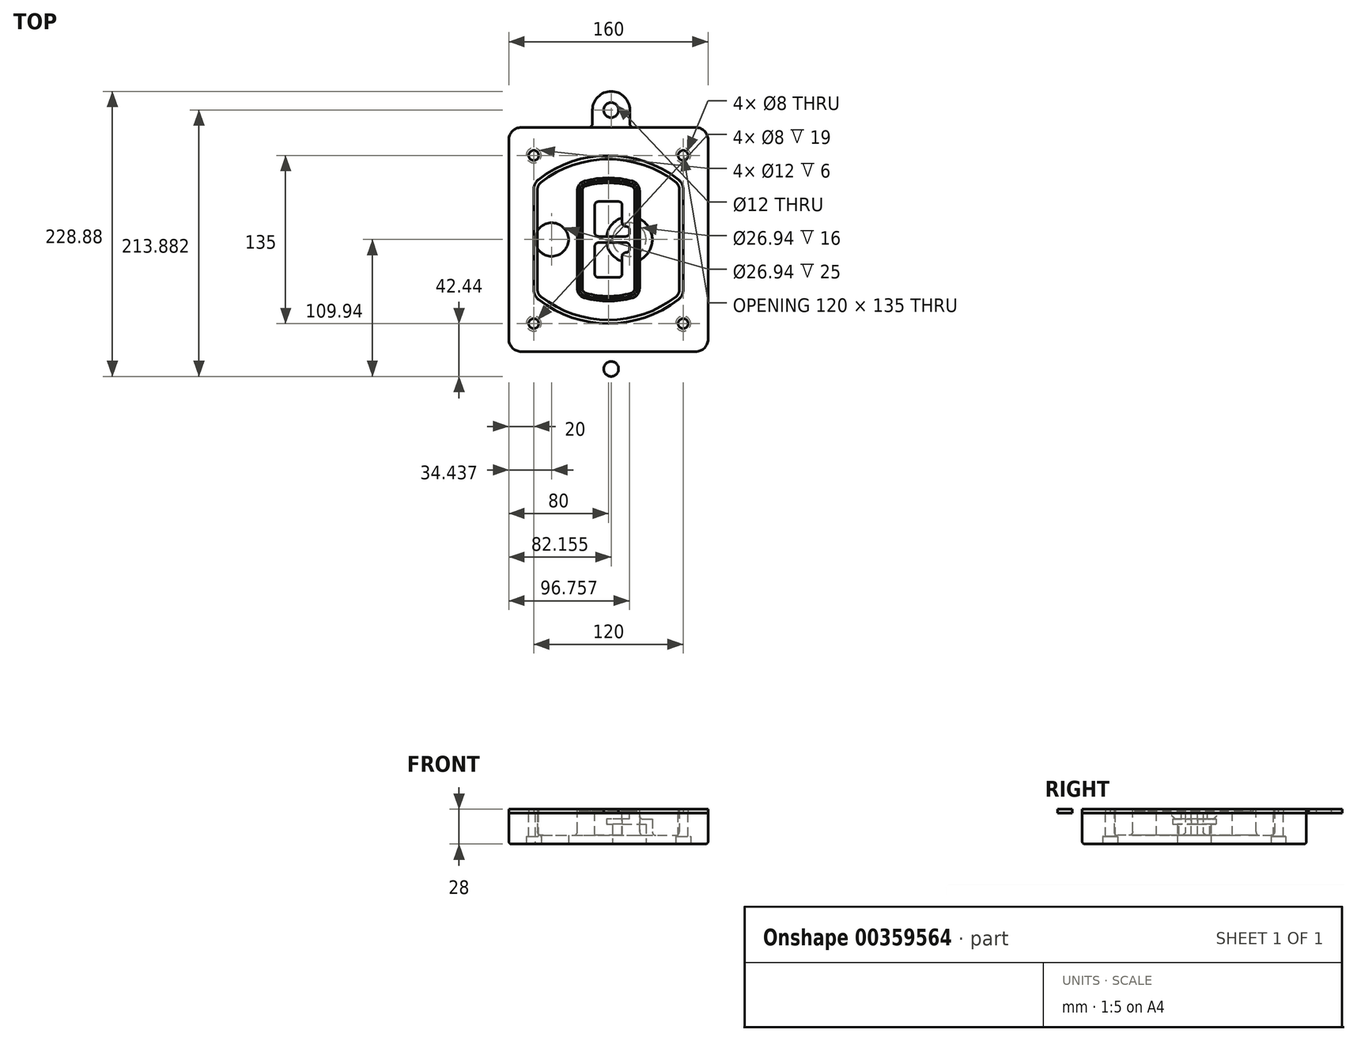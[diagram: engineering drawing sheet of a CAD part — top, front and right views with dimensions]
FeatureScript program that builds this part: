
annotation { "Feature Type Name" : "Feature", "Feature Type Description" : "" }
export const myFeature = defineFeature(function(context is Context, id is Id, definition is map)
    precondition{}
    {
        {
            var Q0;
            Q0=qCreatedBy(makeId("Top.planeOp"),FACE);
            var sketch = newSketch(context, id + "F0", { "sketchPlane" : qUnion([Q0])});
            skPoint(sketch, "E0.rect.middle", {"position": v(0, 0) * mm});
            skLineSegment(sketch, "E1.bottom", {"start": v(-70, -90) * mm, "end": v(70, -90) * mm});
            skLineSegment(sketch, "E1.top", {"start": v(-70, 90) * mm, "end": v(70, 90) * mm});
            skLineSegment(sketch, "E1.left", {"start": v(-80, -80) * mm, "end": v(-80, 80) * mm});
            skLineSegment(sketch, "E1.right", {"start": v(80, -80) * mm, "end": v(80, 80) * mm});
            skLineSegment(sketch, "E2", {"start": v(-80, 90) * mm, "end": v(80, -90) * mm, "construction": true});
            skLineSegment(sketch, "E3", {"start": v(80, 90) * mm, "end": v(-80, -90) * mm, "construction": true});
            skCircle(sketch, "E4", {"center": v(-60, 67.5) * mm, "radius": 4 * mm});
            skCircle(sketch, "E5", {"center": v(60, 67.5) * mm, "radius": 4 * mm});
            skCircle(sketch, "E6", {"center": v(60, -67.5) * mm, "radius": 4 * mm});
            skCircle(sketch, "E7", {"center": v(-60, -67.5) * mm, "radius": 4 * mm});
            skLineSegment(sketch, "E8", {"start": v(-60, 67.5) * mm, "end": v(60, 67.5) * mm, "construction": true});
            skLineSegment(sketch, "E9", {"start": v(60, 67.5) * mm, "end": v(60, -67.5) * mm, "construction": true});
            skLineSegment(sketch, "E10", {"start": v(60, -67.5) * mm, "end": v(-60, -67.5) * mm, "construction": true});
            skLineSegment(sketch, "E11", {"start": v(-60, -67.5) * mm, "end": v(-60, 67.5) * mm, "construction": true});
            skLineSegment(sketch, "E12", {"start": v(-60, 40.3) * mm, "end": v(-60, -40.3) * mm});
            skLineSegment(sketch, "E13", {"start": v(60, 40.3) * mm, "end": v(60, -40.3) * mm});
            skArc(sketch, "E14", {"start": v(56.15, 48.18) * mm, "mid": v(0, 67.5) * mm, "end": v(-56.15, 48.18) * mm});
            skArc(sketch, "E15", {"start": v(-56.15, -48.18) * mm, "mid": v(0, -67.5) * mm, "end": v(56.15, -48.18) * mm});
            skLineSegment(sketch, "E16", {"start": v(-60, 0) * mm, "end": v(60, 0) * mm, "construction": true});
            skPoint(sketch, "E17.visualSharp", {"position": v(-60, -45) * mm});
            skArc(sketch, "E17.filletArc", {"start": v(-60, -40.3) * mm, "mid": v(-58.99, -44.68) * mm, "end": v(-56.15, -48.18) * mm});
            skPoint(sketch, "E18.visualSharp", {"position": v(-60, 45) * mm});
            skArc(sketch, "E18.filletArc", {"start": v(-56.15, 48.18) * mm, "mid": v(-58.99, 44.68) * mm, "end": v(-60, 40.3) * mm});
            skPoint(sketch, "E19.visualSharp", {"position": v(60, 45) * mm});
            skArc(sketch, "E19.filletArc", {"start": v(60, 40.3) * mm, "mid": v(58.99, 44.68) * mm, "end": v(56.15, 48.18) * mm});
            skPoint(sketch, "E20.visualSharp", {"position": v(60, -45) * mm});
            skArc(sketch, "E20.filletArc", {"start": v(56.15, -48.18) * mm, "mid": v(58.99, -44.68) * mm, "end": v(60, -40.3) * mm});
            skPoint(sketch, "E21.visualSharp", {"position": v(-80, 90) * mm});
            skArc(sketch, "E21.filletArc", {"start": v(-70, 90) * mm, "mid": v(-77.07, 87.07) * mm, "end": v(-80, 80) * mm});
            skPoint(sketch, "E22.visualSharp", {"position": v(80, 90) * mm});
            skArc(sketch, "E22.filletArc", {"start": v(80, 80) * mm, "mid": v(77.07, 87.07) * mm, "end": v(70, 90) * mm});
            skPoint(sketch, "E23.visualSharp", {"position": v(80, -90) * mm});
            skArc(sketch, "E23.filletArc", {"start": v(70, -90) * mm, "mid": v(77.07, -87.07) * mm, "end": v(80, -80) * mm});
            skPoint(sketch, "E24.visualSharp", {"position": v(-80, -90) * mm});
            skArc(sketch, "E24.filletArc", {"start": v(-80, -80) * mm, "mid": v(-77.07, -87.07) * mm, "end": v(-70, -90) * mm});
            skArc(sketch, "E25.0", {"start": v(57, 40.3) * mm, "mid": v(56.3, 43.36) * mm, "end": v(54.3, 45.81) * mm});
            skLineSegment(sketch, "E25.1", {"start": v(57, 40.3) * mm, "end": v(57, -40.3) * mm});
            skArc(sketch, "E25.2", {"start": v(54.3, -45.81) * mm, "mid": v(56.3, -43.36) * mm, "end": v(57, -40.3) * mm});
            skArc(sketch, "E25.3", {"start": v(-54.3, -45.81) * mm, "mid": v(0, -64.5) * mm, "end": v(54.3, -45.81) * mm});
            skArc(sketch, "E25.4", {"start": v(-57, -40.3) * mm, "mid": v(-56.3, -43.36) * mm, "end": v(-54.3, -45.81) * mm});
            skArc(sketch, "E25.5", {"start": v(54.3, 45.81) * mm, "mid": v(0, 64.5) * mm, "end": v(-54.3, 45.81) * mm});
            skLineSegment(sketch, "E25.6", {"start": v(-57, 40.3) * mm, "end": v(-57, -40.3) * mm});
            skArc(sketch, "E25.7", {"start": v(-54.3, 45.81) * mm, "mid": v(-56.3, 43.36) * mm, "end": v(-57, 40.3) * mm});
            skArc(sketch, "E26.0", {"start": v(-58.62, 51.33) * mm, "mid": v(-62.58, 46.43) * mm, "end": v(-64, 40.3) * mm});
            skArc(sketch, "E26.1", {"start": v(58.62, 51.33) * mm, "mid": v(0, 71.5) * mm, "end": v(-58.62, 51.33) * mm});
            skArc(sketch, "E26.2", {"start": v(64, 40.3) * mm, "mid": v(62.58, 46.43) * mm, "end": v(58.62, 51.33) * mm});
            skLineSegment(sketch, "E26.3", {"start": v(64, 40.3) * mm, "end": v(64, -40.3) * mm});
            skArc(sketch, "E26.4", {"start": v(58.62, -51.33) * mm, "mid": v(62.58, -46.43) * mm, "end": v(64, -40.3) * mm});
            skLineSegment(sketch, "E26.5", {"start": v(-64, 40.3) * mm, "end": v(-64, -40.3) * mm});
            skArc(sketch, "E26.6", {"start": v(-58.62, -51.33) * mm, "mid": v(0, -71.5) * mm, "end": v(58.62, -51.33) * mm});
            skArc(sketch, "E26.7", {"start": v(-64, -40.3) * mm, "mid": v(-62.58, -46.43) * mm, "end": v(-58.62, -51.33) * mm});
            skSolve(sketch);
        }
        {
            var Q0;
            Q0=makeQuery(id+"F0.imprint","IMPRINT",FACE,{"disambiguationData":[TD([[makeQuery(id+"F0.imprint","IMPRINT",EDGE,{"derivedFrom":sQuery(id+"F0.wireOp",EDGE,"E1.bottom")}),1.0]])]});
            var Q1;
            Q1=makeQuery(id+"F0.imprint","IMPRINT",FACE,{"disambiguationData":[TD([[makeQuery(id+"F0.imprint","IMPRINT",EDGE,{"derivedFrom":sQuery(id+"F0.wireOp",EDGE,"E12")}),1.0]])]});
            var Q2;
            Q2=makeQuery(id+"F0.imprint","IMPRINT",FACE,{"disambiguationData":[TD([[makeQuery(id+"F0.imprint","IMPRINT",EDGE,{"derivedFrom":sQuery(id+"F0.wireOp",EDGE,"E25.0")}),1.0]])]});
            var Q3;
            Q3=makeQuery(id+"F0.imprint","IMPRINT",FACE,{"disambiguationData":[TD([[makeQuery(id+"F0.imprint","IMPRINT",EDGE,{"derivedFrom":sQuery(id+"F0.wireOp",EDGE,"E12")}),-1.0]])]});
            extrude(context, id + "F1", {"entities" : qUnion([Q0, Q1, Q2, Q3]), "oppositeDirection" : true, "depth" : 25 * mm});
        }
        {
            var Q0;
            Q0=makeQuery(id+"F0.imprint","IMPRINT",FACE,{"disambiguationData":[TD([[makeQuery(id+"F0.imprint","IMPRINT",EDGE,{"derivedFrom":sQuery(id+"F0.wireOp",EDGE,"E12")}),1.0]])]});
            extrude(context, id + "F2", {"entities" : qUnion([Q0]), "operationType" : NewBodyOperationType.ADD, "depth" : 3 * mm});
        }
        {
            var Q0;
            Q0=makeQuery(id+"F0.imprint","IMPRINT",FACE,{"disambiguationData":[TD([[makeQuery(id+"F0.imprint","IMPRINT",EDGE,{"derivedFrom":sQuery(id+"F0.wireOp",EDGE,"E25.0")}),1.0]])]});
            extrude(context, id + "F3", {"entities" : qUnion([Q0]), "operationType" : NewBodyOperationType.REMOVE, "oppositeDirection" : true, "depth" : 18 * mm});
        }
        {
            var Q0;
            Q0=makeQuery(id+"F2.opExtrude","CAP_FACE",FACE,{"disambiguationData":[OSD([sQuery(id+"F0.wireOp",EDGE,"E12"),sQuery(id+"F0.wireOp",EDGE,"E13"),sQuery(id+"F0.wireOp",EDGE,"E14"),sQuery(id+"F0.wireOp",EDGE,"E15"),sQuery(id+"F0.wireOp",EDGE,"E17.filletArc"),sQuery(id+"F0.wireOp",EDGE,"E18.filletArc"),sQuery(id+"F0.wireOp",EDGE,"E19.filletArc"),sQuery(id+"F0.wireOp",EDGE,"E20.filletArc"),sQuery(id+"F0.wireOp",EDGE,"E25.0"),sQuery(id+"F0.wireOp",EDGE,"E25.1"),sQuery(id+"F0.wireOp",EDGE,"E25.2"),sQuery(id+"F0.wireOp",EDGE,"E25.3"),sQuery(id+"F0.wireOp",EDGE,"E25.4"),sQuery(id+"F0.wireOp",EDGE,"E25.5"),sQuery(id+"F0.wireOp",EDGE,"E25.6"),sQuery(id+"F0.wireOp",EDGE,"E25.7")])],"isStart":false});
            var sketch = newSketch(context, id + "F4", { "sketchPlane" : qUnion([Q0])});
            skArc(sketch, "E27.0", {"start": v(-19.08, -46.97) * mm, "mid": v(0, -49.5) * mm, "end": v(19.08, -46.97) * mm});
            skArc(sketch, "E28.0", {"start": v(19.08, 46.97) * mm, "mid": v(0, 49.5) * mm, "end": v(-19.08, 46.97) * mm});
            skLineSegment(sketch, "E29", {"start": v(-25, 39.25) * mm, "end": v(-25, -39.25) * mm});
            skLineSegment(sketch, "E30", {"start": v(25, 39.25) * mm, "end": v(25, -39.25) * mm});
            skLineSegment(sketch, "E31", {"start": v(-25, 45.1) * mm, "end": v(25, 45.1) * mm, "construction": true});
            skLineSegment(sketch, "E32", {"start": v(-25, -45.1) * mm, "end": v(25, -45.1) * mm, "construction": true});
            skPoint(sketch, "E33.visualSharp", {"position": v(-25, 45.1) * mm});
            skArc(sketch, "E33.filletArc", {"start": v(-19.08, 46.97) * mm, "mid": v(-23.35, 44.11) * mm, "end": v(-25, 39.25) * mm});
            skPoint(sketch, "E34.visualSharp", {"position": v(25, 45.1) * mm});
            skArc(sketch, "E34.filletArc", {"start": v(25, 39.25) * mm, "mid": v(23.35, 44.11) * mm, "end": v(19.08, 46.97) * mm});
            skPoint(sketch, "E35.visualSharp", {"position": v(25, -45.1) * mm});
            skArc(sketch, "E35.filletArc", {"start": v(19.08, -46.97) * mm, "mid": v(23.35, -44.11) * mm, "end": v(25, -39.25) * mm});
            skPoint(sketch, "E36.visualSharp", {"position": v(-25, -45.1) * mm});
            skArc(sketch, "E36.filletArc", {"start": v(-25, -39.25) * mm, "mid": v(-23.35, -44.11) * mm, "end": v(-19.08, -46.97) * mm});
            skArc(sketch, "E37.0", {"start": v(54.3, 45.81) * mm, "mid": v(0, 64.5) * mm, "end": v(-54.3, 45.81) * mm});
            skArc(sketch, "E37.1", {"start": v(-54.3, 45.81) * mm, "mid": v(-56.3, 43.36) * mm, "end": v(-57, 40.3) * mm});
            skLineSegment(sketch, "E37.2", {"start": v(-57, 40.3) * mm, "end": v(-57, -40.3) * mm});
            skArc(sketch, "E37.3", {"start": v(-57, -40.3) * mm, "mid": v(-56.3, -43.36) * mm, "end": v(-54.3, -45.81) * mm});
            skArc(sketch, "E37.4", {"start": v(-54.3, -45.81) * mm, "mid": v(0, -64.5) * mm, "end": v(54.3, -45.81) * mm});
            skArc(sketch, "E37.5", {"start": v(54.3, -45.81) * mm, "mid": v(56.3, -43.36) * mm, "end": v(57, -40.3) * mm});
            skLineSegment(sketch, "E37.6", {"start": v(57, 40.3) * mm, "end": v(57, -40.3) * mm});
            skArc(sketch, "E37.7", {"start": v(57, 40.3) * mm, "mid": v(56.3, 43.36) * mm, "end": v(54.3, 45.81) * mm});
            skLineSegment(sketch, "E38.0", {"start": v(23, 39.25) * mm, "end": v(23, -39.25) * mm});
            skArc(sketch, "E38.1", {"start": v(18.56, -45.04) * mm, "mid": v(21.76, -42.9) * mm, "end": v(23, -39.25) * mm});
            skArc(sketch, "E38.2", {"start": v(-18.56, -45.04) * mm, "mid": v(0, -47.5) * mm, "end": v(18.56, -45.04) * mm});
            skArc(sketch, "E38.3", {"start": v(-23, -39.25) * mm, "mid": v(-21.76, -42.9) * mm, "end": v(-18.56, -45.04) * mm});
            skLineSegment(sketch, "E38.4", {"start": v(-23, 39.25) * mm, "end": v(-23, -39.25) * mm});
            skArc(sketch, "E38.5", {"start": v(23, 39.25) * mm, "mid": v(21.76, 42.9) * mm, "end": v(18.56, 45.04) * mm});
            skArc(sketch, "E38.6", {"start": v(-18.56, 45.04) * mm, "mid": v(-21.76, 42.9) * mm, "end": v(-23, 39.25) * mm});
            skArc(sketch, "E38.7", {"start": v(18.56, 45.04) * mm, "mid": v(0, 47.5) * mm, "end": v(-18.56, 45.04) * mm});
            skArc(sketch, "E39.0", {"start": v(21, 39.25) * mm, "mid": v(20.18, 41.68) * mm, "end": v(18.04, 43.1) * mm});
            skLineSegment(sketch, "E39.1", {"start": v(21, 39.25) * mm, "end": v(21, -39.25) * mm});
            skArc(sketch, "E39.2", {"start": v(18.04, -43.1) * mm, "mid": v(20.18, -41.68) * mm, "end": v(21, -39.25) * mm});
            skArc(sketch, "E39.3", {"start": v(-18.04, -43.1) * mm, "mid": v(0, -45.5) * mm, "end": v(18.04, -43.1) * mm});
            skArc(sketch, "E39.4", {"start": v(-21, -39.25) * mm, "mid": v(-20.18, -41.68) * mm, "end": v(-18.04, -43.1) * mm});
            skArc(sketch, "E39.5", {"start": v(18.04, 43.1) * mm, "mid": v(0, 45.5) * mm, "end": v(-18.04, 43.1) * mm});
            skLineSegment(sketch, "E39.6", {"start": v(-21, 39.25) * mm, "end": v(-21, -39.25) * mm});
            skArc(sketch, "E39.7", {"start": v(-18.04, 43.1) * mm, "mid": v(-20.18, 41.68) * mm, "end": v(-21, 39.25) * mm});
            skLineSegment(sketch, "E40", {"start": v(-25, 0) * mm, "end": v(25, 0) * mm, "construction": true});
            skLineSegment(sketch, "E41", {"start": v(-11, 5.5) * mm, "end": v(-11, 27.5) * mm});
            skLineSegment(sketch, "E42", {"start": v(-8, 30.5) * mm, "end": v(8, 30.5) * mm});
            skLineSegment(sketch, "E43", {"start": v(11, 27.5) * mm, "end": v(11, 13.5) * mm});
            skLineSegment(sketch, "E44", {"start": v(14, 10.5) * mm, "end": v(14, 10.5) * mm});
            skLineSegment(sketch, "E45", {"start": v(17, 7.5) * mm, "end": v(17, 5.5) * mm});
            skLineSegment(sketch, "E46", {"start": v(14, 2.5) * mm, "end": v(-8, 2.5) * mm});
            skPoint(sketch, "E47.visualSharp", {"position": v(-11, 30.5) * mm});
            skArc(sketch, "E47.filletArc", {"start": v(-8, 30.5) * mm, "mid": v(-10.12, 29.62) * mm, "end": v(-11, 27.5) * mm});
            skPoint(sketch, "E48.visualSharp", {"position": v(11, 30.5) * mm});
            skArc(sketch, "E48.filletArc", {"start": v(11, 27.5) * mm, "mid": v(10.12, 29.62) * mm, "end": v(8, 30.5) * mm});
            skPoint(sketch, "E49.visualSharp", {"position": v(11, 10.5) * mm});
            skArc(sketch, "E49.filletArc", {"start": v(11, 13.5) * mm, "mid": v(11.88, 11.38) * mm, "end": v(14, 10.5) * mm});
            skPoint(sketch, "E50.visualSharp", {"position": v(17, 10.5) * mm});
            skArc(sketch, "E50.filletArc", {"start": v(17, 7.5) * mm, "mid": v(16.12, 9.62) * mm, "end": v(14, 10.5) * mm});
            skPoint(sketch, "E51.visualSharp", {"position": v(17, 2.5) * mm});
            skArc(sketch, "E51.filletArc", {"start": v(14, 2.5) * mm, "mid": v(16.12, 3.38) * mm, "end": v(17, 5.5) * mm});
            skPoint(sketch, "E52.visualSharp", {"position": v(-11, 2.5) * mm});
            skArc(sketch, "E52.filletArc", {"start": v(-11, 5.5) * mm, "mid": v(-10.12, 3.38) * mm, "end": v(-8, 2.5) * mm});
            skLineSegment(sketch, "E53.0.MirrorCS", {"start": v(14, -2.5) * mm, "end": v(-8, -2.5) * mm});
            skArc(sketch, "E54.0.MirrorCS", {"start": v(-11, -5.5) * mm, "mid": v(-10.12, -3.38) * mm, "end": v(-8, -2.5) * mm});
            skLineSegment(sketch, "E55.0.MirrorCS", {"start": v(-11, -5.5) * mm, "end": v(-11, -27.5) * mm});
            skArc(sketch, "E56.0.MirrorCS", {"start": v(-8, -30.5) * mm, "mid": v(-10.12, -29.62) * mm, "end": v(-11, -27.5) * mm});
            skLineSegment(sketch, "E57.0.MirrorCS", {"start": v(-8, -30.5) * mm, "end": v(8, -30.5) * mm});
            skArc(sketch, "E58.0.MirrorCS", {"start": v(11, -27.5) * mm, "mid": v(10.12, -29.62) * mm, "end": v(8, -30.5) * mm});
            skLineSegment(sketch, "E59.0.MirrorCS", {"start": v(11, -27.5) * mm, "end": v(11, -13.5) * mm});
            skArc(sketch, "E60.0.MirrorCS", {"start": v(11, -13.5) * mm, "mid": v(11.88, -11.38) * mm, "end": v(14, -10.5) * mm});
            skArc(sketch, "E61.0.MirrorCS", {"start": v(17, -7.5) * mm, "mid": v(16.12, -9.62) * mm, "end": v(14, -10.5) * mm});
            skLineSegment(sketch, "E62.0.MirrorCS", {"start": v(17, -7.5) * mm, "end": v(17, -5.5) * mm});
            skArc(sketch, "E63.0.MirrorCS", {"start": v(14, -2.5) * mm, "mid": v(16.12, -3.38) * mm, "end": v(17, -5.5) * mm});
            skSolve(sketch);
        }
        {
            var Q0;
            Q0=makeQuery(id+"F4.imprint","IMPRINT",FACE,{"disambiguationData":[TD([[makeQuery(id+"F4.imprint","IMPRINT",EDGE,{"derivedFrom":sQuery(id+"F4.wireOp",EDGE,"E27.0")}),1.0]])]});
            var Q1;
            Q1=makeQuery(id+"F4.imprint","IMPRINT",FACE,{"disambiguationData":[TD([[makeQuery(id+"F4.imprint","IMPRINT",EDGE,{"derivedFrom":sQuery(id+"F4.wireOp",EDGE,"E38.0")}),-1.0]])]});
            var Q2;
            Q2=makeQuery(id+"F4.imprint","IMPRINT",FACE,{"disambiguationData":[TD([[makeQuery(id+"F4.imprint","IMPRINT",EDGE,{"derivedFrom":sQuery(id+"F4.wireOp",EDGE,"E39.0")}),1.0]])]});
            extrude(context, id + "F5", {"entities" : qUnion([Q0, Q1, Q2]), "operationType" : NewBodyOperationType.ADD, "endBound" : BoundingType.UP_TO_NEXT, "oppositeDirection" : true, "depth" : 25 * mm});
        }
        {
            var Q0;
            Q0=makeQuery(id+"F4.imprint","IMPRINT",FACE,{"disambiguationData":[TD([[makeQuery(id+"F4.imprint","IMPRINT",EDGE,{"derivedFrom":sQuery(id+"F4.wireOp",EDGE,"E38.0")}),-1.0]])]});
            extrude(context, id + "F6", {"entities" : qUnion([Q0]), "operationType" : NewBodyOperationType.REMOVE, "oppositeDirection" : true, "depth" : 2 * mm});
        }
        {
            var Q0;
            Q0=makeQuery(id+"F1.opExtrude","CAP_FACE",FACE,{"disambiguationData":[OSD([sQuery(id+"F0.wireOp",EDGE,"E1.bottom"),sQuery(id+"F0.wireOp",EDGE,"E1.top"),sQuery(id+"F0.wireOp",EDGE,"E1.left"),sQuery(id+"F0.wireOp",EDGE,"E1.right"),sQuery(id+"F0.wireOp",EDGE,"E4"),sQuery(id+"F0.wireOp",EDGE,"E5"),sQuery(id+"F0.wireOp",EDGE,"E6"),sQuery(id+"F0.wireOp",EDGE,"E7"),sQuery(id+"F0.wireOp",EDGE,"E21.filletArc"),sQuery(id+"F0.wireOp",EDGE,"E22.filletArc"),sQuery(id+"F0.wireOp",EDGE,"E23.filletArc"),sQuery(id+"F0.wireOp",EDGE,"E24.filletArc")])],"isStart":false});
            var sketch = newSketch(context, id + "F7", { "sketchPlane" : qUnion([Q0])});
            skCircle(sketch, "E64", {"center": v(16.76, 0) * mm, "radius": 13.47 * mm});
            skCircle(sketch, "E65", {"center": v(-45.56, 0) * mm, "radius": 13.47 * mm});
            skLineSegment(sketch, "E66", {"start": v(80, 0) * mm, "end": v(-80, 0) * mm});
            skCircle(sketch, "E67", {"center": v(16.76, 0) * mm, "radius": 18.47 * mm});
            skCircle(sketch, "E68", {"center": v(60, -67.5) * mm, "radius": 6 * mm});
            skCircle(sketch, "E69", {"center": v(-60, -67.5) * mm, "radius": 6 * mm});
            skCircle(sketch, "E70", {"center": v(-60, 67.5) * mm, "radius": 6 * mm});
            skCircle(sketch, "E71", {"center": v(60, 67.5) * mm, "radius": 6 * mm});
            skSolve(sketch);
        }
        {
            var Q0;
            {var subQ1=sQuery(id+"F7.wireOp",EDGE,"E66");var subQ4=sQuery(id+"F7.wireOp",EDGE,"E64");var subQ6=makeQuery(id+"F7.imprint","INTERSECT",VERTEX,{"disambiguationData":[OD(0.0)],"derivedFrom":[subQ4,subQ1]});Q0=makeQuery(id+"F7.imprint","IMPRINT",FACE,{"disambiguationData":[TD([[makeQuery(id+"F7.imprint","IMPRINT",EDGE,{"disambiguationData":[TD([[subQ6,-1.0]])],"derivedFrom":subQ4}),-1.0]])]});}
            var Q1;
            {var subQ0=sQuery(id+"F7.wireOp",EDGE,"E66");var subQ1=sQuery(id+"F7.wireOp",EDGE,"E64");var subQ3=makeQuery(id+"F7.imprint","INTERSECT",VERTEX,{"disambiguationData":[OD(0.0)],"derivedFrom":[subQ1,subQ0]});Q1=makeQuery(id+"F7.imprint","IMPRINT",FACE,{"disambiguationData":[TD([[makeQuery(id+"F7.imprint","IMPRINT",EDGE,{"disambiguationData":[TD([[subQ3,-1.0]])],"derivedFrom":subQ1}),1.0]])]});}
            var Q2;
            {var subQ0=sQuery(id+"F7.wireOp",EDGE,"E66");var subQ1=sQuery(id+"F7.wireOp",EDGE,"E64");var subQ3=makeQuery(id+"F7.imprint","INTERSECT",VERTEX,{"disambiguationData":[OD(0.0)],"derivedFrom":[subQ1,subQ0]});Q2=makeQuery(id+"F7.imprint","IMPRINT",FACE,{"disambiguationData":[TD([[makeQuery(id+"F7.imprint","IMPRINT",EDGE,{"disambiguationData":[TD([[subQ3,1.0]])],"derivedFrom":subQ1}),1.0]])]});}
            var Q3;
            {var subQ1=sQuery(id+"F7.wireOp",EDGE,"E66");var subQ4=sQuery(id+"F7.wireOp",EDGE,"E64");var subQ6=makeQuery(id+"F7.imprint","INTERSECT",VERTEX,{"disambiguationData":[OD(0.0)],"derivedFrom":[subQ4,subQ1]});Q3=makeQuery(id+"F7.imprint","IMPRINT",FACE,{"disambiguationData":[TD([[makeQuery(id+"F7.imprint","IMPRINT",EDGE,{"disambiguationData":[TD([[subQ6,1.0]])],"derivedFrom":subQ4}),-1.0]])]});}
            extrude(context, id + "F8", {"entities" : qUnion([Q0, Q1, Q2, Q3]), "operationType" : NewBodyOperationType.ADD, "oppositeDirection" : true, "depth" : 20 * mm});
        }
        {
            var Q0;
            {var subQ0=sQuery(id+"F7.wireOp",EDGE,"E66");var subQ1=sQuery(id+"F7.wireOp",EDGE,"E64");var subQ3=makeQuery(id+"F7.imprint","INTERSECT",VERTEX,{"disambiguationData":[OD(0.0)],"derivedFrom":[subQ1,subQ0]});Q0=makeQuery(id+"F7.imprint","IMPRINT",FACE,{"disambiguationData":[TD([[makeQuery(id+"F7.imprint","IMPRINT",EDGE,{"disambiguationData":[TD([[subQ3,-1.0]])],"derivedFrom":subQ1}),1.0]])]});}
            var Q1;
            {var subQ0=sQuery(id+"F7.wireOp",EDGE,"E66");var subQ1=sQuery(id+"F7.wireOp",EDGE,"E64");var subQ3=makeQuery(id+"F7.imprint","INTERSECT",VERTEX,{"disambiguationData":[OD(0.0)],"derivedFrom":[subQ1,subQ0]});Q1=makeQuery(id+"F7.imprint","IMPRINT",FACE,{"disambiguationData":[TD([[makeQuery(id+"F7.imprint","IMPRINT",EDGE,{"disambiguationData":[TD([[subQ3,1.0]])],"derivedFrom":subQ1}),1.0]])]});}
            extrude(context, id + "F9", {"entities" : qUnion([Q0, Q1]), "operationType" : NewBodyOperationType.REMOVE, "oppositeDirection" : true, "depth" : 16 * mm});
        }
        {
            var Q0;
            {var subQ0=sQuery(id+"F7.wireOp",EDGE,"E66");var subQ1=sQuery(id+"F7.wireOp",EDGE,"E65");var subQ3=makeQuery(id+"F7.imprint","INTERSECT",VERTEX,{"disambiguationData":[OD(0.0)],"derivedFrom":[subQ1,subQ0]});Q0=makeQuery(id+"F7.imprint","IMPRINT",FACE,{"disambiguationData":[TD([[makeQuery(id+"F7.imprint","IMPRINT",EDGE,{"disambiguationData":[TD([[subQ3,-1.0]])],"derivedFrom":subQ1}),1.0]])]});}
            var Q1;
            {var subQ0=sQuery(id+"F7.wireOp",EDGE,"E66");var subQ1=sQuery(id+"F7.wireOp",EDGE,"E65");var subQ3=makeQuery(id+"F7.imprint","INTERSECT",VERTEX,{"disambiguationData":[OD(0.0)],"derivedFrom":[subQ1,subQ0]});Q1=makeQuery(id+"F7.imprint","IMPRINT",FACE,{"disambiguationData":[TD([[makeQuery(id+"F7.imprint","IMPRINT",EDGE,{"disambiguationData":[TD([[subQ3,1.0]])],"derivedFrom":subQ1}),1.0]])]});}
            extrude(context, id + "F10", {"entities" : qUnion([Q0, Q1]), "operationType" : NewBodyOperationType.REMOVE, "oppositeDirection" : true, "depth" : 25 * mm});
        }
        {
            var Q0;
            Q0=makeQuery(id+"F7.imprint","IMPRINT",FACE,{"disambiguationData":[TD([[makeQuery(id+"F7.imprint","IMPRINT",EDGE,{"derivedFrom":sQuery(id+"F7.wireOp",EDGE,"E68")}),1.0]])]});
            var Q1;
            Q1=makeQuery(id+"F7.imprint","IMPRINT",FACE,{"disambiguationData":[TD([[makeQuery(id+"F7.imprint","IMPRINT",EDGE,{"derivedFrom":makeQuery(id+"F1.opExtrude","CAP_EDGE",EDGE,{"disambiguationData":[OSD([sQuery(id+"F0.wireOp",EDGE,"E5")])],"isStart":false})}),-1.0]])]});
            var Q2;
            Q2=makeQuery(id+"F7.imprint","IMPRINT",FACE,{"disambiguationData":[TD([[makeQuery(id+"F7.imprint","IMPRINT",EDGE,{"derivedFrom":sQuery(id+"F7.wireOp",EDGE,"E69")}),1.0]])]});
            var Q3;
            Q3=makeQuery(id+"F7.imprint","IMPRINT",FACE,{"disambiguationData":[TD([[makeQuery(id+"F7.imprint","IMPRINT",EDGE,{"derivedFrom":makeQuery(id+"F1.opExtrude","CAP_EDGE",EDGE,{"disambiguationData":[OSD([sQuery(id+"F0.wireOp",EDGE,"E4")])],"isStart":false})}),-1.0]])]});
            var Q4;
            Q4=makeQuery(id+"F7.imprint","IMPRINT",FACE,{"disambiguationData":[TD([[makeQuery(id+"F7.imprint","IMPRINT",EDGE,{"derivedFrom":sQuery(id+"F7.wireOp",EDGE,"E70")}),1.0]])]});
            var Q5;
            Q5=makeQuery(id+"F7.imprint","IMPRINT",FACE,{"disambiguationData":[TD([[makeQuery(id+"F7.imprint","IMPRINT",EDGE,{"derivedFrom":makeQuery(id+"F1.opExtrude","CAP_EDGE",EDGE,{"disambiguationData":[OSD([sQuery(id+"F0.wireOp",EDGE,"E7")])],"isStart":false})}),-1.0]])]});
            var Q6;
            Q6=makeQuery(id+"F7.imprint","IMPRINT",FACE,{"disambiguationData":[TD([[makeQuery(id+"F7.imprint","IMPRINT",EDGE,{"derivedFrom":sQuery(id+"F7.wireOp",EDGE,"E71")}),1.0]])]});
            var Q7;
            Q7=makeQuery(id+"F7.imprint","IMPRINT",FACE,{"disambiguationData":[TD([[makeQuery(id+"F7.imprint","IMPRINT",EDGE,{"derivedFrom":makeQuery(id+"F1.opExtrude","CAP_EDGE",EDGE,{"disambiguationData":[OSD([sQuery(id+"F0.wireOp",EDGE,"E6")])],"isStart":false})}),-1.0]])]});
            extrude(context, id + "F11", {"entities" : qUnion([Q0, Q1, Q2, Q3, Q4, Q5, Q6, Q7]), "operationType" : NewBodyOperationType.REMOVE, "oppositeDirection" : true, "depth" : 6 * mm});
        }
        {
            var Q0;
            Q0=makeQuery(id+"F9.boolean.opBoolean","COPY",FACE,{"derivedFrom":makeQuery(id+"F9.opExtrude","CAP_FACE",FACE,{"disambiguationData":[OSD([sQuery(id+"F7.wireOp",EDGE,"E64")])],"isStart":false})});
            var sketch = newSketch(context, id + "F12", { "sketchPlane" : qUnion([Q0])});
            skArc(sketch, "E72.0", {"start": v(11, 17.55) * mm, "mid": v(2.57, 11.82) * mm, "end": v(-1.54, 2.5) * mm});
            skArc(sketch, "E72.1", {"start": v(-1.54, -2.5) * mm, "mid": v(2.57, -11.82) * mm, "end": v(11, -17.55) * mm});
            skLineSegment(sketch, "E73", {"start": v(-1.54, -2.5) * mm, "end": v(14, -2.5) * mm});
            skLineSegment(sketch, "E74.0", {"start": v(14, 2.5) * mm, "end": v(-1.54, 2.5) * mm});
            skArc(sketch, "E74.1", {"start": v(14, 2.5) * mm, "mid": v(16.12, 3.38) * mm, "end": v(17, 5.5) * mm});
            skLineSegment(sketch, "E74.2", {"start": v(17, 7.5) * mm, "end": v(17, 5.5) * mm});
            skArc(sketch, "E74.3", {"start": v(17, 7.5) * mm, "mid": v(16.12, 9.62) * mm, "end": v(14, 10.5) * mm});
            skArc(sketch, "E74.4", {"start": v(11, 13.5) * mm, "mid": v(11.88, 11.38) * mm, "end": v(14, 10.5) * mm});
            skLineSegment(sketch, "E74.5", {"start": v(11, 17.55) * mm, "end": v(11, 13.5) * mm});
            skLineSegment(sketch, "E74.7", {"start": v(14, -2.5) * mm, "end": v(-1.54, -2.5) * mm});
            skArc(sketch, "E74.8", {"start": v(14, -2.5) * mm, "mid": v(16.12, -3.38) * mm, "end": v(17, -5.5) * mm});
            skLineSegment(sketch, "E74.9", {"start": v(17, -7.5) * mm, "end": v(17, -5.5) * mm});
            skArc(sketch, "E74.10", {"start": v(17, -7.5) * mm, "mid": v(16.12, -9.62) * mm, "end": v(14, -10.5) * mm});
            skArc(sketch, "E74.11", {"start": v(11, -13.5) * mm, "mid": v(11.88, -11.38) * mm, "end": v(14, -10.5) * mm});
            skLineSegment(sketch, "E74.12", {"start": v(11, -17.55) * mm, "end": v(11, -13.5) * mm});
            skPoint(sketch, "E75.orphan", {"position": v(11, -27.5) * mm});
            skPoint(sketch, "E76.orphan", {"position": v(-8, -2.5) * mm});
            skPoint(sketch, "E77.orphan", {"position": v(-8, 2.5) * mm});
            skPoint(sketch, "E78.orphan", {"position": v(11, 27.5) * mm});
            skSolve(sketch);
        }
        {
            var Q0;
            {var subQ7=sQuery(id+"F12.wireOp",EDGE,"E72.0");var subQ14=sQuery(id+"F12.wireOp",EDGE,"E72.1");var subQ16=sQuery(id+"F12.wireOp",EDGE,"E74.1");var subQ18=sQuery(id+"F12.wireOp",EDGE,"E74.8");Q0=qUnion([makeQuery(id+"F12.imprint","IMPRINT",FACE,{"disambiguationData":[TD([[makeQuery(id+"F12.imprint","IMPRINT",EDGE,{"derivedFrom":subQ7}),1.0]])]}),makeQuery(id+"F12.imprint","IMPRINT",FACE,{"disambiguationData":[TD([[makeQuery(id+"F12.imprint","IMPRINT",EDGE,{"derivedFrom":subQ14}),1.0]])]}),makeQuery(id+"F12.imprint","IMPRINT",FACE,{"disambiguationData":[TD([[makeQuery(id+"F12.imprint","IMPRINT",EDGE,{"derivedFrom":subQ16}),1.0]])]}),makeQuery(id+"F12.imprint","IMPRINT",FACE,{"disambiguationData":[TD([[makeQuery(id+"F12.imprint","IMPRINT",EDGE,{"derivedFrom":subQ18}),-1.0]])]})]);}
            var Q1;
            Q1=makeQuery(id+"F5.boolean.opBoolean","SPLIT",FACE,{"disambiguationData":[TD([makeQuery(id+"F5.opExtrude","SWEPT_FACE",FACE,{"disambiguationData":[OSD([sQuery(id+"F4.wireOp",EDGE,"E41")])]})])],"derivedFrom":makeQuery(id+"F3.boolean.opBoolean","COPY",FACE,{"derivedFrom":makeQuery(id+"F3.opExtrude","CAP_FACE",FACE,{"disambiguationData":[OSD([sQuery(id+"F0.wireOp",EDGE,"E25.0"),sQuery(id+"F0.wireOp",EDGE,"E25.1"),sQuery(id+"F0.wireOp",EDGE,"E25.2"),sQuery(id+"F0.wireOp",EDGE,"E25.3"),sQuery(id+"F0.wireOp",EDGE,"E25.4"),sQuery(id+"F0.wireOp",EDGE,"E25.5"),sQuery(id+"F0.wireOp",EDGE,"E25.6"),sQuery(id+"F0.wireOp",EDGE,"E25.7")])],"isStart":false})})});
            extrude(context, id + "F13", {"entities" : qUnion([Q0]), "operationType" : NewBodyOperationType.REMOVE, "endBound" : BoundingType.UP_TO_SURFACE, "endBoundEntityFace" : qUnion([Q1]), "depth" : 25 * mm});
        }
        {
            var Q0;
            Q0=makeQuery(id+"F3.boolean.opBoolean","COPY",EDGE,{"derivedFrom":makeQuery(id+"F3.opExtrude","CAP_EDGE",EDGE,{"disambiguationData":[OSD([sQuery(id+"F0.wireOp",EDGE,"E25.6")])],"isStart":false})});
            var Q1;
            Q1=makeQuery(id+"F8.boolean.opBoolean","INTERSECT",EDGE,{"derivedFrom":[makeQuery(id+"F5.opExtrude","SWEPT_FACE",FACE,{"disambiguationData":[OSD([sQuery(id+"F4.wireOp",EDGE,"E30")])]}),makeQuery(id+"F8.opExtrude","CAP_FACE",FACE,{"disambiguationData":[OSD([sQuery(id+"F7.wireOp",EDGE,"E67")])],"isStart":false})]});
            var Q2;
            Q2=makeQuery(id+"F8.boolean.opBoolean","INTERSECT",EDGE,{"disambiguationData":[OD(1.0)],"derivedFrom":[makeQuery(id+"F5.opExtrude","SWEPT_FACE",FACE,{"disambiguationData":[OSD([sQuery(id+"F4.wireOp",EDGE,"E30")])]}),makeQuery(id+"F8.opExtrude","SWEPT_FACE",FACE,{"disambiguationData":[OSD([sQuery(id+"F7.wireOp",EDGE,"E67")])]})]});
            var Q3;
            {var subQ0=sQuery(id+"F4.wireOp",EDGE,"E30");Q3=makeQuery(id+"F8.boolean.opBoolean","SPLIT",EDGE,{"disambiguationData":[TD([makeQuery(id+"F5.opExtrude","SWEPT_FACE",FACE,{"disambiguationData":[OSD([sQuery(id+"F4.wireOp",EDGE,"E35.filletArc")])]})])],"derivedFrom":makeQuery(id+"F5.opExtrude","CAP_EDGE",EDGE,{"disambiguationData":[OSD([subQ0])],"isStart":false})});}
            var Q4;
            {var subQ0=sQuery(id+"F0.wireOp",EDGE,"E25.7");var subQ1=sQuery(id+"F0.wireOp",EDGE,"E25.1");var subQ2=sQuery(id+"F0.wireOp",EDGE,"E25.6");var subQ3=sQuery(id+"F0.wireOp",EDGE,"E25.5");var subQ4=sQuery(id+"F0.wireOp",EDGE,"E25.4");var subQ5=sQuery(id+"F0.wireOp",EDGE,"E25.0");var subQ6=sQuery(id+"F0.wireOp",EDGE,"E25.2");var subQ7=sQuery(id+"F0.wireOp",EDGE,"E25.3");Q4=makeQuery(id+"F8.boolean.opBoolean","INTERSECT",EDGE,{"derivedFrom":[makeQuery(id+"F5.boolean.opBoolean","SPLIT",FACE,{"disambiguationData":[TD([makeQuery(id+"F2.opExtrude","SWEPT_FACE",FACE,{"disambiguationData":[OSD([subQ5])]})])],"derivedFrom":makeQuery(id+"F3.boolean.opBoolean","COPY",FACE,{"derivedFrom":makeQuery(id+"F3.opExtrude","CAP_FACE",FACE,{"disambiguationData":[OSD([subQ5,subQ1,subQ6,subQ7,subQ4,subQ3,subQ2,subQ0])],"isStart":false})})}),makeQuery(id+"F8.opExtrude","SWEPT_FACE",FACE,{"disambiguationData":[OSD([sQuery(id+"F7.wireOp",EDGE,"E67")])]})]});}
            var Q5;
            Q5=makeQuery(id+"F8.boolean.opBoolean","INTERSECT",EDGE,{"disambiguationData":[OD(0.0)],"derivedFrom":[makeQuery(id+"F5.opExtrude","SWEPT_FACE",FACE,{"disambiguationData":[OSD([sQuery(id+"F4.wireOp",EDGE,"E30")])]}),makeQuery(id+"F8.opExtrude","SWEPT_FACE",FACE,{"disambiguationData":[OSD([sQuery(id+"F7.wireOp",EDGE,"E67")])]})]});
            fillet(context, id + "F14", {"entities" : qUnion([Q0, Q1, Q2, Q3, Q4, Q5]), "radius" : 3 * mm, "tangentPropagation" : true, "allowEdgeOverflow" : false});
        }
        {
            var Q0;
            Q0=makeQuery(id+"F1.opExtrude","CAP_EDGE",EDGE,{"disambiguationData":[OSD([sQuery(id+"F0.wireOp",EDGE,"E1.bottom")])],"isStart":false});
            fillet(context, id + "F15", {"entities" : qUnion([Q0]), "radius" : 2 * mm, "tangentPropagation" : true, "allowEdgeOverflow" : false});
        }
        {
            var Q0;
            {var subQ0=sQuery(id+"F0.wireOp",EDGE,"E21.filletArc");var subQ1=sQuery(id+"F0.wireOp",EDGE,"E7");var subQ2=sQuery(id+"F0.wireOp",EDGE,"E6");var subQ3=sQuery(id+"F0.wireOp",EDGE,"E5");var subQ4=sQuery(id+"F0.wireOp",EDGE,"E4");var subQ5=sQuery(id+"F0.wireOp",EDGE,"E22.filletArc");var subQ6=sQuery(id+"F0.wireOp",EDGE,"E1.bottom");var subQ7=sQuery(id+"F0.wireOp",EDGE,"E1.right");var subQ8=sQuery(id+"F0.wireOp",EDGE,"E1.top");var subQ9=sQuery(id+"F0.wireOp",EDGE,"E1.left");var subQ10=sQuery(id+"F0.wireOp",EDGE,"E23.filletArc");var subQ11=sQuery(id+"F0.wireOp",EDGE,"E24.filletArc");Q0=makeQuery(id+"F2.boolean.opBoolean","SPLIT",FACE,{"disambiguationData":[TD([makeQuery(id+"F1.opExtrude","SWEPT_FACE",FACE,{"disambiguationData":[OSD([subQ6])]})])],"derivedFrom":makeQuery(id+"F1.opExtrude","CAP_FACE",FACE,{"disambiguationData":[OSD([subQ6,subQ8,subQ9,subQ7,subQ4,subQ3,subQ2,subQ1,subQ0,subQ5,subQ10,subQ11])],"isStart":true})});}
            var sketch = newSketch(context, id + "F16", { "sketchPlane" : qUnion([Q0])});
            skSolve(sketch);
        }
        {
            var Q0;
            Q0=makeQuery(id+"F16.imprint","IMPRINT",FACE,{"disambiguationData":[TD([[makeQuery(id+"F16.imprint","IMPRINT",EDGE,{"derivedFrom":makeQuery(id+"F1.opExtrude","CAP_EDGE",EDGE,{"disambiguationData":[OSD([sQuery(id+"F0.wireOp",EDGE,"E1.bottom")])],"isStart":true})}),1.0]])]});
            var sketch = newSketch(context, id + "F17", { "sketchPlane" : qUnion([Q0])});
            skCircle(sketch, "E79", {"center": v(2.15, 103.94) * mm, "radius": 6 * mm});
            skLineSegment(sketch, "E80", {"start": v(-43.8, 73.94) * mm, "end": v(48.1, 73.94) * mm});
            skLineSegment(sketch, "E81", {"start": v(-30.85, 73.94) * mm, "end": v(-12.85, 91.94) * mm});
            skLineSegment(sketch, "E82", {"start": v(35.15, 73.94) * mm, "end": v(17.15, 91.94) * mm});
            skLineSegment(sketch, "E83", {"start": v(-12.85, 91.94) * mm, "end": v(-12.85, 103.94) * mm});
            skLineSegment(sketch, "E84", {"start": v(17.15, 91.94) * mm, "end": v(17.15, 103.94) * mm});
            skArc(sketch, "E85", {"start": v(-12.85, 103.94) * mm, "mid": v(2.15, 118.94) * mm, "end": v(17.15, 103.94) * mm});
            skLineSegment(sketch, "E86", {"start": v(2.15, 73.94) * mm, "end": v(2.15, 133.57) * mm, "construction": true});
            skLineSegment(sketch, "E87", {"start": v(-74.96, 0) * mm, "end": v(74.57, 0) * mm, "construction": true});
            skLineSegment(sketch, "E88.MirrorCS", {"start": v(-12.85, -91.94) * mm, "end": v(-12.85, -103.94) * mm});
            skArc(sketch, "E89.MirrorCS", {"start": v(-12.85, -103.94) * mm, "mid": v(2.15, -118.94) * mm, "end": v(17.15, -103.94) * mm});
            skCircle(sketch, "E90.MirrorC", {"center": v(2.15, -103.94) * mm, "radius": 6 * mm});
            skLineSegment(sketch, "E91.MirrorCS", {"start": v(17.15, -91.94) * mm, "end": v(17.15, -103.94) * mm});
            skLineSegment(sketch, "E92.MirrorCS", {"start": v(-30.85, -73.94) * mm, "end": v(-12.85, -91.94) * mm});
            skLineSegment(sketch, "E93.MirrorCS", {"start": v(35.15, -73.94) * mm, "end": v(17.15, -91.94) * mm});
            skLineSegment(sketch, "E94.MirrorCS", {"start": v(2.15, -73.94) * mm, "end": v(2.15, -133.57) * mm, "construction": true});
            skSolve(sketch);
        }
        {
            var Q0;
            Q0=makeQuery(id+"F17.imprint","IMPRINT",FACE,{"disambiguationData":[TD([[makeQuery(id+"F17.imprint","IMPRINT",EDGE,{"derivedFrom":sQuery(id+"F17.wireOp",EDGE,"E79")}),-1.0]])]});
            var Q1;
            Q1=makeQuery(id+"F17.imprint","IMPRINT",FACE,{"disambiguationData":[TD([[makeQuery(id+"F17.imprint","IMPRINT",EDGE,{"derivedFrom":sQuery(id+"F17.wireOp",EDGE,"E90.MirrorC")}),1.0]])]});
            var Q2;
            Q2=makeQuery(id+"F16.imprint","IMPRINT",FACE,{"disambiguationData":[TD([[makeQuery(id+"F16.imprint","IMPRINT",EDGE,{"derivedFrom":makeQuery(id+"F1.opExtrude","CAP_EDGE",EDGE,{"disambiguationData":[OSD([sQuery(id+"F0.wireOp",EDGE,"E1.bottom")])],"isStart":true})}),1.0]])]});
            var Q3;
            Q3=makeQuery(id+"F2.opExtrude","CAP_FACE",FACE,{"disambiguationData":[OSD([sQuery(id+"F0.wireOp",EDGE,"E12"),sQuery(id+"F0.wireOp",EDGE,"E13"),sQuery(id+"F0.wireOp",EDGE,"E14"),sQuery(id+"F0.wireOp",EDGE,"E15"),sQuery(id+"F0.wireOp",EDGE,"E17.filletArc"),sQuery(id+"F0.wireOp",EDGE,"E18.filletArc"),sQuery(id+"F0.wireOp",EDGE,"E19.filletArc"),sQuery(id+"F0.wireOp",EDGE,"E20.filletArc"),sQuery(id+"F0.wireOp",EDGE,"E25.0"),sQuery(id+"F0.wireOp",EDGE,"E25.1"),sQuery(id+"F0.wireOp",EDGE,"E25.2"),sQuery(id+"F0.wireOp",EDGE,"E25.3"),sQuery(id+"F0.wireOp",EDGE,"E25.4"),sQuery(id+"F0.wireOp",EDGE,"E25.5"),sQuery(id+"F0.wireOp",EDGE,"E25.6"),sQuery(id+"F0.wireOp",EDGE,"E25.7")])],"isStart":false});
            extrude(context, id + "F18", {"entities" : qUnion([Q0, Q1, Q2]), "endBound" : BoundingType.UP_TO_SURFACE, "endBoundEntityFace" : qUnion([Q3]), "depth" : 25 * mm});
        }
    });
